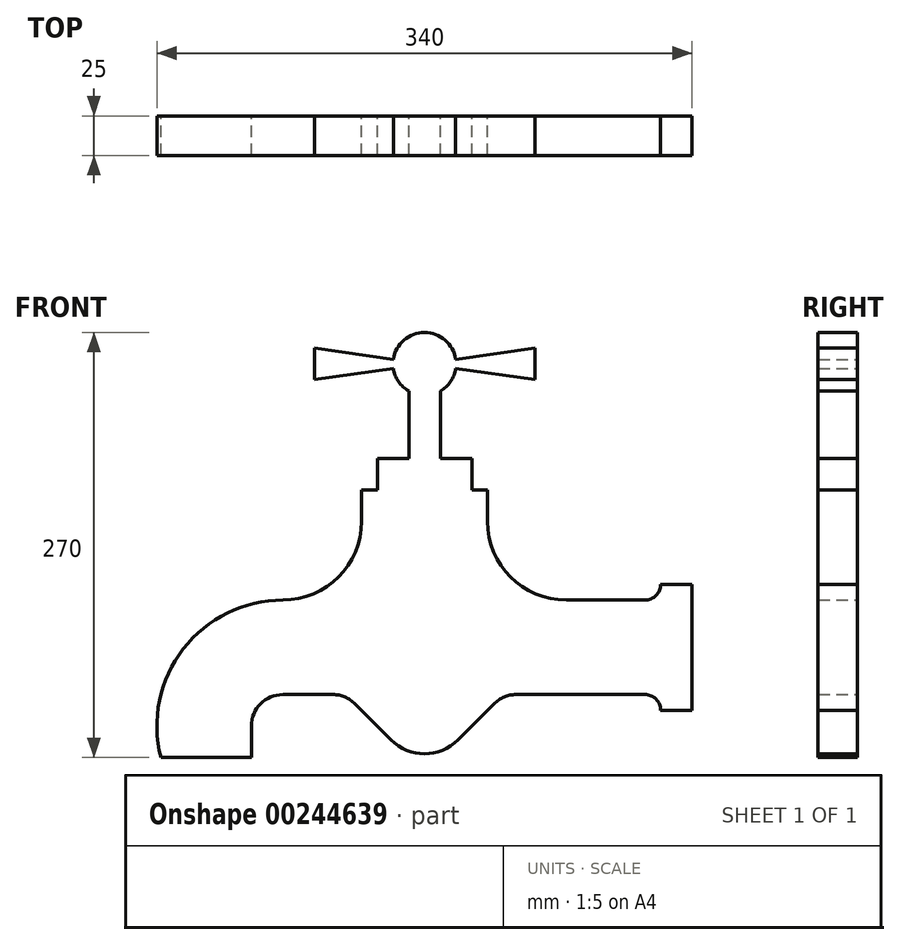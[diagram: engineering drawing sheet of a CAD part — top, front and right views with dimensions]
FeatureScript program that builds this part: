
annotation { "Feature Type Name" : "Feature", "Feature Type Description" : "" }
export const myFeature = defineFeature(function(context is Context, id is Id, definition is map)
    precondition{}
    {
        {
            var Q0;
            Q0=qCreatedBy(makeId("Front.planeOp"),FACE);
            var sketch = newSketch(context, id + "F0", { "sketchPlane" : qUnion([Q0])});
            skLineSegment(sketch, "E0", {"start": v(0, 140) * mm, "end": v(0, -103.7) * mm, "construction": true});
            skLineSegment(sketch, "E1", {"start": v(90, 45.95) * mm, "end": v(90, -47.82) * mm, "construction": true});
            skLineSegment(sketch, "E2", {"start": v(-90, 53.2) * mm, "end": v(-90, -53.45) * mm, "construction": true});
            skLineSegment(sketch, "E3", {"start": v(-40, 140) * mm, "end": v(40, 140) * mm});
            skLineSegment(sketch, "E4", {"start": v(-40, 140) * mm, "end": v(-40, 120) * mm});
            skArc(sketch, "E5", {"start": v(-90, 70) * mm, "mid": v(-54.64, 84.64) * mm, "end": v(-40, 120) * mm});
            skArc(sketch, "E6", {"start": v(-90, 70) * mm, "mid": v(-153.25, 38.99) * mm, "end": v(-167.46, -30) * mm});
            skLineSegment(sketch, "E7", {"start": v(-30, 140) * mm, "end": v(-30, 160) * mm});
            skLineSegment(sketch, "E8", {"start": v(-30, 160) * mm, "end": v(30, 160) * mm});
            skLineSegment(sketch, "E9", {"start": v(30, 160) * mm, "end": v(30, 140) * mm});
            skLineSegment(sketch, "E10", {"start": v(40, 140) * mm, "end": v(40, 120) * mm});
            skArc(sketch, "E11", {"start": v(40, 120) * mm, "mid": v(54.64, 84.64) * mm, "end": v(90, 70) * mm});
            skLineSegment(sketch, "E12", {"start": v(-205.2, -10) * mm, "end": v(247.2, -10) * mm, "construction": true});
            skLineSegment(sketch, "E13", {"start": v(-170, -10) * mm, "end": v(-170, -30) * mm});
            skArc(sketch, "E14", {"start": v(-90, 10) * mm, "mid": v(-104.14, 4.14) * mm, "end": v(-110, -10) * mm});
            skLineSegment(sketch, "E15", {"start": v(-110, -10) * mm, "end": v(-110, -30) * mm});
            skLineSegment(sketch, "E16", {"start": v(-110, -30) * mm, "end": v(-170, -30) * mm});
            skLineSegment(sketch, "E17", {"start": v(-90, 10) * mm, "end": v(-58.28, 10) * mm});
            skLineSegment(sketch, "E18", {"start": v(-44.14, 4.14) * mm, "end": v(-21.21, -18.79) * mm});
            skLineSegment(sketch, "E19", {"start": v(21.21, -18.79) * mm, "end": v(44.14, 4.14) * mm});
            skLineSegment(sketch, "E20", {"start": v(58.28, 10) * mm, "end": v(140, 10) * mm});
            skLineSegment(sketch, "E21", {"start": v(150, 0) * mm, "end": v(150, 0) * mm});
            skLineSegment(sketch, "E22", {"start": v(150, 0) * mm, "end": v(170, 0) * mm});
            skLineSegment(sketch, "E23", {"start": v(170, 0) * mm, "end": v(170, 80) * mm});
            skLineSegment(sketch, "E24", {"start": v(170, 80) * mm, "end": v(150, 80) * mm});
            skLineSegment(sketch, "E25", {"start": v(90, 70) * mm, "end": v(140, 70) * mm});
            skLineSegment(sketch, "E26", {"start": v(150, 80) * mm, "end": v(150, 80) * mm});
            skPoint(sketch, "E27.visualSharp", {"position": v(0, -40) * mm});
            skArc(sketch, "E27.filletArc", {"start": v(-21.21, -18.79) * mm, "mid": v(0, -27.57) * mm, "end": v(21.21, -18.79) * mm});
            skPoint(sketch, "E28.visualSharp", {"position": v(-50, 10) * mm});
            skArc(sketch, "E28.filletArc", {"start": v(-44.14, 4.14) * mm, "mid": v(-50.63, 8.48) * mm, "end": v(-58.28, 10) * mm});
            skPoint(sketch, "E29.visualSharp", {"position": v(50, 10) * mm});
            skArc(sketch, "E29.filletArc", {"start": v(58.28, 10) * mm, "mid": v(50.63, 8.48) * mm, "end": v(44.14, 4.14) * mm});
            skArc(sketch, "E30", {"start": v(10, 202.68) * mm, "mid": v(0, 240) * mm, "end": v(-10, 202.68) * mm});
            skPoint(sketch, "E30.centerSnap0", {"position": v(0, 160) * mm});
            skLineSegment(sketch, "E31", {"start": v(10, 160) * mm, "end": v(10, 202.68) * mm});
            skLineSegment(sketch, "E32", {"start": v(-10, 202.68) * mm, "end": v(-10, 160) * mm});
            skLineSegment(sketch, "E33", {"start": v(19.8, 222.83) * mm, "end": v(70, 230) * mm});
            skLineSegment(sketch, "E34", {"start": v(70, 230) * mm, "end": v(70, 210) * mm});
            skLineSegment(sketch, "E35", {"start": v(70, 210) * mm, "end": v(19.8, 217.17) * mm});
            skLineSegment(sketch, "E36.MirrorCS", {"start": v(-70, 230) * mm, "end": v(-70, 210) * mm});
            skLineSegment(sketch, "E37.MirrorCS", {"start": v(-19.8, 222.83) * mm, "end": v(-70, 230) * mm});
            skLineSegment(sketch, "E38.MirrorCS", {"start": v(-70, 210) * mm, "end": v(-19.8, 217.17) * mm});
            skLineSegment(sketch, "E39", {"start": v(20, 220) * mm, "end": v(171.1, 220) * mm, "construction": true});
            skPoint(sketch, "E40.visualSharp", {"position": v(150, 10) * mm});
            skArc(sketch, "E40.filletArc", {"start": v(150, 0) * mm, "mid": v(147.07, 7.07) * mm, "end": v(140, 10) * mm});
            skPoint(sketch, "E41.visualSharp", {"position": v(150, 70) * mm});
            skArc(sketch, "E41.filletArc", {"start": v(140, 70) * mm, "mid": v(147.07, 72.93) * mm, "end": v(150, 80) * mm});
            skSolve(sketch);
        }
        {
            var Q0;
            {var subQ8=sQuery(id+"F0.wireOp",EDGE,"E4");Q0=makeQuery(id+"F0.imprint","IMPRINT",FACE,{"disambiguationData":[TD([[makeQuery(id+"F0.imprint","IMPRINT",EDGE,{"derivedFrom":subQ8}),1.0]])]});}
            var Q1;
            {var subQ3=sQuery(id+"F0.wireOp",EDGE,"E7");Q1=makeQuery(id+"F0.imprint","IMPRINT",FACE,{"disambiguationData":[TD([[makeQuery(id+"F0.imprint","IMPRINT",EDGE,{"derivedFrom":subQ3}),-1.0]])]});}
            var Q2;
            {var subQ4=sQuery(id+"F0.wireOp",EDGE,"E31");Q2=makeQuery(id+"F0.imprint","IMPRINT",FACE,{"disambiguationData":[TD([[makeQuery(id+"F0.imprint","IMPRINT",EDGE,{"derivedFrom":subQ4}),1.0]])]});}
            var Q3;
            {var subQ0=sQuery(id+"F0.wireOp",EDGE,"E33");Q3=makeQuery(id+"F0.imprint","IMPRINT",FACE,{"disambiguationData":[TD([[makeQuery(id+"F0.imprint","IMPRINT",EDGE,{"derivedFrom":subQ0}),-1.0]])]});}
            var Q4;
            Q4=makeQuery(id+"F0.imprint","IMPRINT",FACE,{"disambiguationData":[TD([[makeQuery(id+"F0.imprint","IMPRINT",EDGE,{"derivedFrom":sQuery(id+"F0.wireOp",EDGE,"E36.MirrorCS")}),1.0]])]});
            extrude(context, id + "F1", {"entities" : qUnion([Q0, Q1, Q2, Q3, Q4]), "depth" : 25 * mm});
        }
    });
